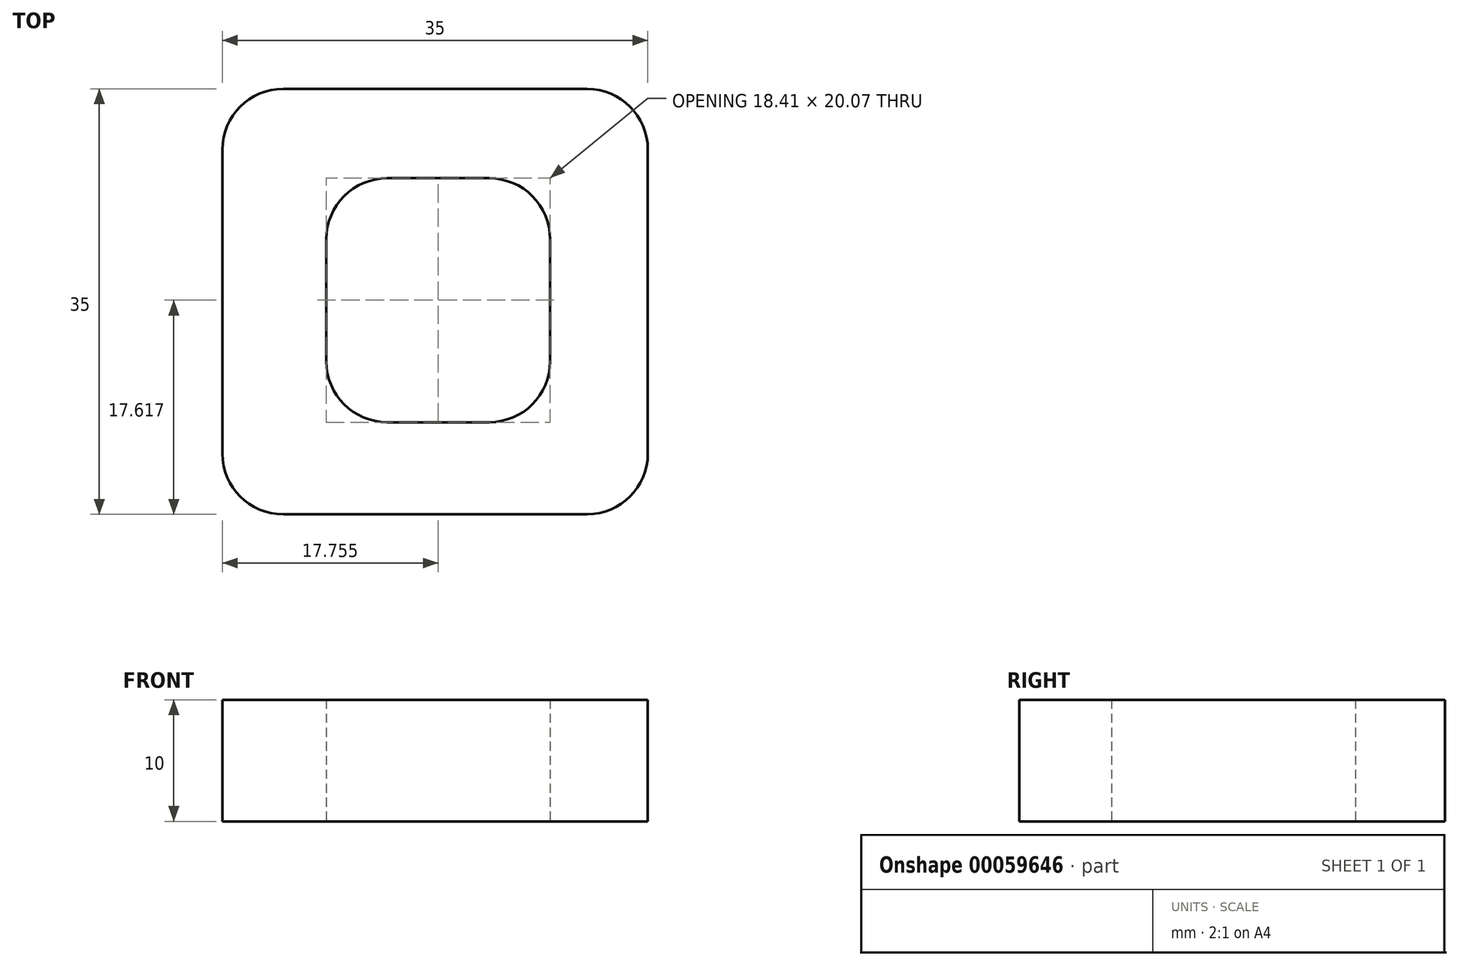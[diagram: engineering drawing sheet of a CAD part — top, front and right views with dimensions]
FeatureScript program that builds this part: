
annotation { "Feature Type Name" : "Feature", "Feature Type Description" : "" }
export const myFeature = defineFeature(function(context is Context, id is Id, definition is map)
    precondition{}
    {
        {
            var Q0;
            Q0=qCreatedBy(makeId("Top.planeOp"),FACE);
            var sketch = newSketch(context, id + "F0", { "sketchPlane" : qUnion([Q0])});
            skLineSegment(sketch, "E0.bottom", {"start": v(-47.97, 42.3) * mm, "end": v(-12.97, 42.3) * mm});
            skLineSegment(sketch, "E0.top", {"start": v(-47.97, 7.3) * mm, "end": v(-12.97, 7.3) * mm});
            skLineSegment(sketch, "E0.left", {"start": v(-47.97, 42.3) * mm, "end": v(-47.97, 7.3) * mm});
            skLineSegment(sketch, "E0.right", {"start": v(-12.97, 42.3) * mm, "end": v(-12.97, 7.3) * mm});
            skSolve(sketch);
        }
        {
            var Q0;
            Q0 = qSketchRegion(id + "F0", true);
            extrude(context, id + "F1", {"entities" : qUnion([Q0]), "depth" : 10 * mm});
        }
        {
            var Q0;
            Q0=qCreatedBy(makeId("Top.planeOp"),FACE);
            var sketch = newSketch(context, id + "F2", { "sketchPlane" : qUnion([Q0])});
            skLineSegment(sketch, "E1.bottom", {"start": v(-39.42, 34.95) * mm, "end": v(-21.01, 34.95) * mm});
            skLineSegment(sketch, "E1.top", {"start": v(-39.42, 14.88) * mm, "end": v(-21.01, 14.88) * mm});
            skLineSegment(sketch, "E1.left", {"start": v(-39.42, 34.95) * mm, "end": v(-39.42, 14.88) * mm});
            skLineSegment(sketch, "E1.right", {"start": v(-21.01, 34.95) * mm, "end": v(-21.01, 14.88) * mm});
            skSolve(sketch);
        }
        {
            var Q0;
            Q0 = qSketchRegion(id + "F2", true);
            extrude(context, id + "F3", {"entities" : qUnion([Q0]), "operationType" : NewBodyOperationType.REMOVE, "depth" : 25 * mm});
        }
        {
            var Q0;
            Q0=makeQuery(id+"F1.opExtrude","SWEPT_EDGE",EDGE,{"disambiguationData":[OSD([sQuery(id+"F0.wireOp",EDGE,"E0.bottom"),sQuery(id+"F0.wireOp",EDGE,"E0.right")])]});
            var Q1;
            Q1=makeQuery(id+"F1.opExtrude","SWEPT_EDGE",EDGE,{"disambiguationData":[OSD([sQuery(id+"F0.wireOp",EDGE,"E0.bottom"),sQuery(id+"F0.wireOp",EDGE,"E0.left")])]});
            var Q2;
            Q2=makeQuery(id+"F1.opExtrude","SWEPT_EDGE",EDGE,{"disambiguationData":[OSD([sQuery(id+"F0.wireOp",EDGE,"E0.top"),sQuery(id+"F0.wireOp",EDGE,"E0.left")])]});
            var Q3;
            Q3=makeQuery(id+"F1.opExtrude","SWEPT_EDGE",EDGE,{"disambiguationData":[OSD([sQuery(id+"F0.wireOp",EDGE,"E0.top"),sQuery(id+"F0.wireOp",EDGE,"E0.right")])]});
            var Q4;
            Q4=makeQuery(id+"F3.boolean.opBoolean","COPY",EDGE,{"derivedFrom":makeQuery(id+"F3.opExtrude","SWEPT_EDGE",EDGE,{"disambiguationData":[OSD([sQuery(id+"F2.wireOp",EDGE,"E1.top"),sQuery(id+"F2.wireOp",EDGE,"E1.right")])]})});
            var Q5;
            Q5=makeQuery(id+"F3.boolean.opBoolean","COPY",EDGE,{"derivedFrom":makeQuery(id+"F3.opExtrude","SWEPT_EDGE",EDGE,{"disambiguationData":[OSD([sQuery(id+"F2.wireOp",EDGE,"E1.top"),sQuery(id+"F2.wireOp",EDGE,"E1.left")])]})});
            var Q6;
            Q6=makeQuery(id+"F3.boolean.opBoolean","COPY",EDGE,{"derivedFrom":makeQuery(id+"F3.opExtrude","SWEPT_EDGE",EDGE,{"disambiguationData":[OSD([sQuery(id+"F2.wireOp",EDGE,"E1.bottom"),sQuery(id+"F2.wireOp",EDGE,"E1.left")])]})});
            var Q7;
            Q7=makeQuery(id+"F3.boolean.opBoolean","COPY",EDGE,{"derivedFrom":makeQuery(id+"F3.opExtrude","SWEPT_EDGE",EDGE,{"disambiguationData":[OSD([sQuery(id+"F2.wireOp",EDGE,"E1.bottom"),sQuery(id+"F2.wireOp",EDGE,"E1.right")])]})});
            fillet(context, id + "F4", {"entities" : qUnion([Q0, Q1, Q2, Q3, Q4, Q5, Q6, Q7]), "radius" : 5 * mm, "tangentPropagation" : true, "allowEdgeOverflow" : false});
        }
    });
